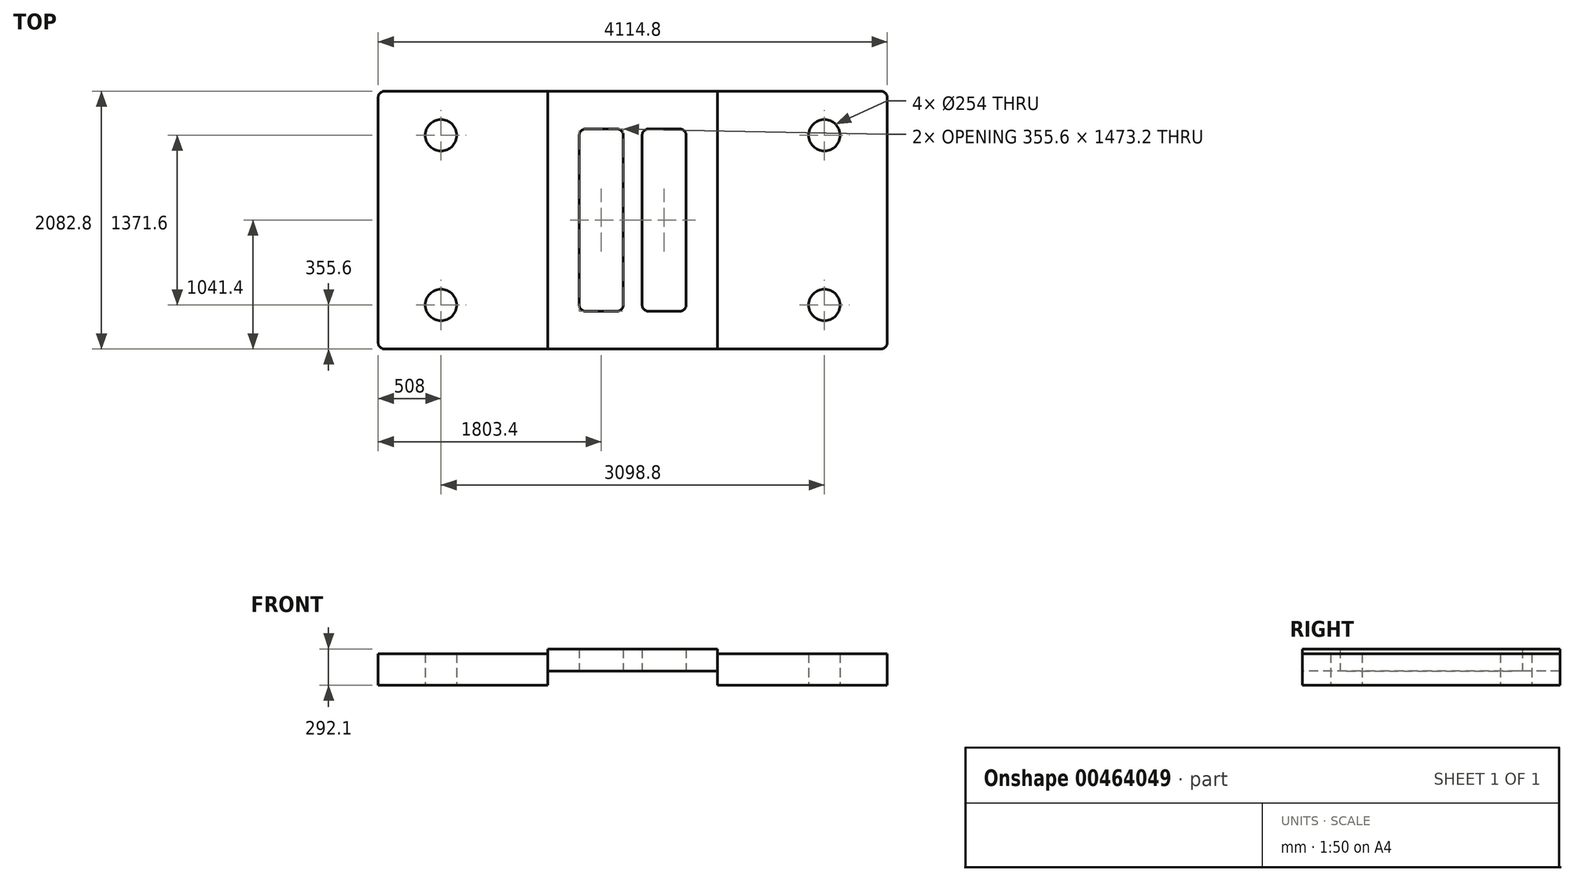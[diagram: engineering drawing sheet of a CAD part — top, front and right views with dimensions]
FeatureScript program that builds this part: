
annotation { "Feature Type Name" : "Feature", "Feature Type Description" : "" }
export const myFeature = defineFeature(function(context is Context, id is Id, definition is map)
    precondition{}
    {
        {
            var Q0;
            Q0=qCreatedBy(makeId("Top.planeOp"),FACE);
            var sketch = newSketch(context, id + "F0", { "sketchPlane" : qUnion([Q0])});
            skLineSegment(sketch, "E0.bottom", {"start": v(2006.6, 1041.4) * mm, "end": v(-2006.6, 1041.4) * mm});
            skLineSegment(sketch, "E0.top", {"start": v(2006.6, -1041.4) * mm, "end": v(-2006.6, -1041.4) * mm});
            skLineSegment(sketch, "E0.left", {"start": v(2057.4, 990.6) * mm, "end": v(2057.4, -990.6) * mm});
            skLineSegment(sketch, "E0.right", {"start": v(-2057.4, 990.6) * mm, "end": v(-2057.4, -990.6) * mm});
            skPoint(sketch, "E0.middle", {"position": v(0, 0) * mm});
            skLineSegment(sketch, "E1", {"start": v(0, 0) * mm, "end": v(0, 1041.4) * mm, "construction": true});
            skPoint(sketch, "E2.visualSharp", {"position": v(2057.4, 1041.4) * mm});
            skArc(sketch, "E2.filletArc", {"start": v(2057.4, 990.6) * mm, "mid": v(2042.52, 1026.52) * mm, "end": v(2006.6, 1041.4) * mm});
            skLineSegment(sketch, "E3", {"start": v(0, 0) * mm, "end": v(0, -1041.4) * mm, "construction": true});
            skLineSegment(sketch, "E4", {"start": v(0, 0) * mm, "end": v(-2057.4, 0) * mm, "construction": true});
            skLineSegment(sketch, "E5", {"start": v(0, 0) * mm, "end": v(2057.4, 0) * mm, "construction": true});
            skPoint(sketch, "E6.visualSharp", {"position": v(2057.4, -1041.4) * mm});
            skArc(sketch, "E6.filletArc", {"start": v(2006.6, -1041.4) * mm, "mid": v(2042.52, -1026.52) * mm, "end": v(2057.4, -990.6) * mm});
            skPoint(sketch, "E7.visualSharp", {"position": v(-2057.4, -1041.4) * mm});
            skArc(sketch, "E7.filletArc", {"start": v(-2057.4, -990.6) * mm, "mid": v(-2042.52, -1026.52) * mm, "end": v(-2006.6, -1041.4) * mm});
            skPoint(sketch, "E8.visualSharp", {"position": v(-2057.4, 1041.4) * mm});
            skArc(sketch, "E8.filletArc", {"start": v(-2006.6, 1041.4) * mm, "mid": v(-2042.52, 1026.52) * mm, "end": v(-2057.4, 990.6) * mm});
            skLineSegment(sketch, "E9", {"start": v(2042.52, -1026.52) * mm, "end": v(-2042.52, 1026.52) * mm, "construction": true});
            skLineSegment(sketch, "E10", {"start": v(-1549.4, 0) * mm, "end": v(-1549.4, 685.8) * mm, "construction": true});
            skLineSegment(sketch, "E11.MirrorCS", {"start": v(-1549.4, 0) * mm, "end": v(-1549.4, -685.8) * mm, "construction": true});
            skLineSegment(sketch, "E12.MirrorCS", {"start": v(1549.4, 0) * mm, "end": v(1549.4, 685.8) * mm, "construction": true});
            skLineSegment(sketch, "E13.MirrorCS", {"start": v(1549.4, 0) * mm, "end": v(1549.4, -685.8) * mm, "construction": true});
            skCircle(sketch, "E14", {"center": v(-1549.4, 685.8) * mm, "radius": 127 * mm});
            skCircle(sketch, "E15.MirrorC", {"center": v(-1549.4, -685.8) * mm, "radius": 127 * mm});
            skCircle(sketch, "E16.MirrorC", {"center": v(1549.4, 685.8) * mm, "radius": 127 * mm});
            skCircle(sketch, "E17.MirrorC", {"center": v(1549.4, -685.8) * mm, "radius": 127 * mm});
            skLineSegment(sketch, "E18", {"start": v(0, 642.72) * mm, "end": v(-685.8, 642.72) * mm, "construction": true});
            skLineSegment(sketch, "E19", {"start": v(0, 642.72) * mm, "end": v(685.8, 642.72) * mm, "construction": true});
            skLineSegment(sketch, "E20", {"start": v(-685.8, 1041.4) * mm, "end": v(-685.8, -1041.4) * mm});
            skLineSegment(sketch, "E21", {"start": v(685.8, 1041.4) * mm, "end": v(685.8, -1041.4) * mm});
            skLineSegment(sketch, "E22", {"start": v(0, 894.4) * mm, "end": v(-76.2, 894.4) * mm, "construction": true});
            skLineSegment(sketch, "E23", {"start": v(0, 894.4) * mm, "end": v(76.2, 894.4) * mm, "construction": true});
            skLineSegment(sketch, "E24", {"start": v(-76.2, 1041.4) * mm, "end": v(-76.2, -1041.4) * mm, "construction": true});
            skLineSegment(sketch, "E25", {"start": v(76.2, 1041.4) * mm, "end": v(76.2, -685.8) * mm, "construction": true});
            skLineSegment(sketch, "E26.bottom", {"start": v(127, 736.6) * mm, "end": v(381, 736.6) * mm});
            skLineSegment(sketch, "E26.top", {"start": v(127, -736.6) * mm, "end": v(381, -736.6) * mm});
            skLineSegment(sketch, "E26.left", {"start": v(76.2, 685.8) * mm, "end": v(76.2, -736.6) * mm});
            skLineSegment(sketch, "E26.right", {"start": v(431.8, 685.8) * mm, "end": v(431.8, -685.8) * mm});
            skLineSegment(sketch, "E27.MirrorCS", {"start": v(-76.2, 685.8) * mm, "end": v(-76.2, -685.8) * mm});
            skLineSegment(sketch, "E28.MirrorCS", {"start": v(-127, 736.6) * mm, "end": v(-381, 736.6) * mm});
            skLineSegment(sketch, "E29.MirrorCS", {"start": v(-431.8, 685.8) * mm, "end": v(-431.8, -685.8) * mm});
            skLineSegment(sketch, "E30.MirrorCS", {"start": v(-127, -736.6) * mm, "end": v(-381, -736.6) * mm});
            skPoint(sketch, "E31.visualSharp", {"position": v(-431.8, 736.6) * mm});
            skArc(sketch, "E31.filletArc", {"start": v(-381, 736.6) * mm, "mid": v(-416.92, 721.72) * mm, "end": v(-431.8, 685.8) * mm});
            skPoint(sketch, "E32.visualSharp", {"position": v(-76.2, 736.6) * mm});
            skArc(sketch, "E32.filletArc", {"start": v(-76.2, 685.8) * mm, "mid": v(-91.08, 721.72) * mm, "end": v(-127, 736.6) * mm});
            skPoint(sketch, "E33.visualSharp", {"position": v(-431.8, -736.6) * mm});
            skArc(sketch, "E33.filletArc", {"start": v(-431.8, -685.8) * mm, "mid": v(-416.92, -721.72) * mm, "end": v(-381, -736.6) * mm});
            skPoint(sketch, "E34.visualSharp", {"position": v(-76.2, -736.6) * mm});
            skArc(sketch, "E34.filletArc", {"start": v(-127, -736.6) * mm, "mid": v(-91.08, -721.72) * mm, "end": v(-76.2, -685.8) * mm});
            skPoint(sketch, "E35.visualSharp", {"position": v(76.2, 736.6) * mm});
            skArc(sketch, "E35.filletArc", {"start": v(127, 736.6) * mm, "mid": v(91.08, 721.72) * mm, "end": v(76.2, 685.8) * mm});
            skPoint(sketch, "E36.visualSharp", {"position": v(431.8, 736.6) * mm});
            skArc(sketch, "E36.filletArc", {"start": v(431.8, 685.8) * mm, "mid": v(416.92, 721.72) * mm, "end": v(381, 736.6) * mm});
            skPoint(sketch, "E37.visualSharp", {"position": v(431.8, -736.6) * mm});
            skArc(sketch, "E37.filletArc", {"start": v(381, -736.6) * mm, "mid": v(416.92, -721.72) * mm, "end": v(431.8, -685.8) * mm});
            skPoint(sketch, "E38.newPointA", {"position": v(76.2, -736.6) * mm});
            skArc(sketch, "E38.filletArc", {"start": v(76.2, -685.8) * mm, "mid": v(91.08, -721.72) * mm, "end": v(127, -736.6) * mm});
            skSolve(sketch);
        }
        {
            var Q0;
            Q0=makeQuery(id+"F0.imprint","IMPRINT",FACE,{"disambiguationData":[TD([[makeQuery(id+"F0.imprint","IMPRINT",EDGE,{"derivedFrom":sQuery(id+"F0.wireOp",EDGE,"E0.left")}),-1.0]])]});
            var Q1;
            Q1=makeQuery(id+"F0.imprint","IMPRINT",FACE,{"disambiguationData":[TD([[makeQuery(id+"F0.imprint","IMPRINT",EDGE,{"derivedFrom":sQuery(id+"F0.wireOp",EDGE,"E0.right")}),1.0]])]});
            extrude(context, id + "F1", {"entities" : qUnion([Q0, Q1]), "depth" : 254 * mm, "symmetric" : true});
        }
        {
            var Q0;
            {var subQ3=sQuery(id+"F0.wireOp",EDGE,"E20");Q0=makeQuery(id+"F0.imprint","IMPRINT",FACE,{"disambiguationData":[TD([[makeQuery(id+"F0.imprint","IMPRINT",EDGE,{"derivedFrom":subQ3}),1.0]])]});}
            extrude(context, id + "F2", {"entities" : qUnion([Q0]), "depth" : 330.2 * mm, "symmetric" : true});
        }
        {
            var Q0;
            Q0=makeQuery(id+"F2.opExtrude","SWEPT_FACE",FACE,{"disambiguationData":[OSD([sQuery(id+"F0.wireOp",EDGE,"E0.top")])]});
            var sketch = newSketch(context, id + "F3", { "sketchPlane" : qUnion([Q0])});
            skLineSegment(sketch, "E39", {"start": v(-685.8, -12.7) * mm, "end": v(685.8, -12.7) * mm});
            skSolve(sketch);
        }
        {
            var Q0;
            {var subQ0=sQuery(id+"F3.wireOp",EDGE,"E39");Q0=makeQuery(id+"F3.imprint","IMPRINT",FACE,{"disambiguationData":[TD([[makeQuery(id+"F3.imprint","IMPRINT",EDGE,{"derivedFrom":subQ0}),-1.0]])]});}
            extrude(context, id + "F4", {"entities" : qUnion([Q0]), "operationType" : NewBodyOperationType.REMOVE, "endBound" : BoundingType.THROUGH_ALL, "oppositeDirection" : true, "depth" : 25.4 * mm});
        }
    });
